# Revit family: TAG3
name_source: partatom
category: Furniture
units: mm (PartAtom-declared; Revit-internal decimal feet)

## family parameters
Always vertical = Yes
Cut with Voids When Loaded = No
OmniClass Number = 23.40.20.00
OmniClass Title = General Furniture and Specialties
Render Appearance Source = Family Geometry
Room Calculation Point = No
Shared = No
Work Plane-Based = No

## types (1)
- CBCGTYP002
    Cost = 20641 $
    Default Elevation = 0 mm  [stored 0 ft]
    Description = 1 x Desktop Organizer - White, 1 x Worksurface Rect 18"D X 42"W X 1 1/8"Th, 1 x FLSP F - Female 1 End - 12D, 1 x FLSP A - Male 1 End Flush - 12D, 1 x CBX HA E 2-Leg base with WS SQ Edge 30d x 66w, 1 x Cbx Full Depth Bbf Ped 18dx28hx16w, 1 x Cb Wall Mounted Cabinet Double Height 14dx32hx36w, 1 x Cbx Suspended Hat Modesty 12h For 54w (38 Actual), 1 x CBX HAT Base E Bookcase No Side Access 21h x 30w x 18d, 1 x CBX HAT BASE E 24", 2 x CBX Wall Mounted L Shelf Vertical 32Hx36Wx12D, 1 x Cbx Full Depth Lat Bf 18dx21hx36w, 1 x Cbx Tackboard Wall Mount 20hx42w, 1 x Cbx Tackboard Wall Mount 28hx66w
    Exported From CET Designer = Yes
    Manufacturer = AIS
    Model = A-DO
    Show CBCGTYP002 = Yes
    VisibilityIndex = 0

note: [stored X ft] marks values corroborated as IEEE doubles in the binary element streams (Revit-internal decimal feet)

## geometry (parser evidence)
native form markers: Sweep x3
no freeform markers — native parametric forms only
